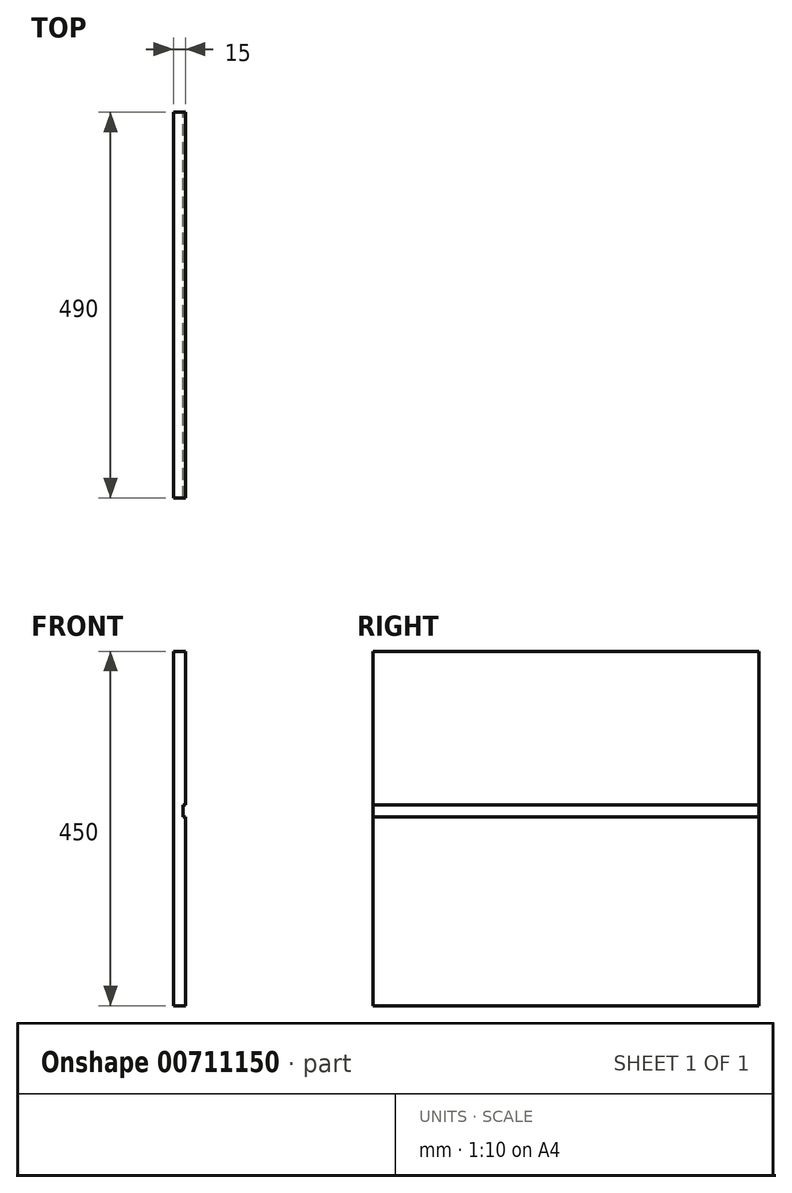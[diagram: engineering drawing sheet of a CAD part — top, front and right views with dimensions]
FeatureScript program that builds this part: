
annotation { "Feature Type Name" : "Feature", "Feature Type Description" : "" }
export const myFeature = defineFeature(function(context is Context, id is Id, definition is map)
    precondition{}
    {
        {
            var Q0;
            Q0=qCreatedBy(makeId("Right.planeOp"),FACE);
            var sketch = newSketch(context, id + "F0", { "sketchPlane" : qUnion([Q0])});
            skLineSegment(sketch, "E0.bottom", {"start": v(0, 0) * mm, "end": v(490, 0) * mm});
            skLineSegment(sketch, "E0.top", {"start": v(0, 450) * mm, "end": v(490, 450) * mm});
            skLineSegment(sketch, "E0.left", {"start": v(0, 0) * mm, "end": v(0, 450) * mm});
            skLineSegment(sketch, "E0.right", {"start": v(490, 0) * mm, "end": v(490, 450) * mm});
            skSolve(sketch);
        }
        {
            var Q0;
            Q0=makeQuery(id+"F0.imprint","IMPRINT",FACE,{"disambiguationData":[TD([[makeQuery(id+"F0.imprint","IMPRINT",EDGE,{"derivedFrom":sQuery(id+"F0.wireOp",EDGE,"E0.bottom")}),1.0]])]});
            extrude(context, id + "F1", {"entities" : qUnion([Q0]), "depth" : 15 * mm, "offsetDistance" : 25 * mm});
        }
        {
            var Q0;
            Q0=makeQuery(id+"F1.opExtrude","CAP_FACE",FACE,{"disambiguationData":[OSD([sQuery(id+"F0.wireOp",EDGE,"E0.bottom"),sQuery(id+"F0.wireOp",EDGE,"E0.top"),sQuery(id+"F0.wireOp",EDGE,"E0.left"),sQuery(id+"F0.wireOp",EDGE,"E0.right")])],"isStart":false});
            var sketch = newSketch(context, id + "F2", { "sketchPlane" : qUnion([Q0])});
            skLineSegment(sketch, "E1.bottom", {"start": v(0, 255) * mm, "end": v(490, 255) * mm});
            skLineSegment(sketch, "E1.top", {"start": v(0, 240) * mm, "end": v(490, 240) * mm});
            skLineSegment(sketch, "E1.left", {"start": v(0, 255) * mm, "end": v(0, 240) * mm});
            skLineSegment(sketch, "E1.right", {"start": v(490, 255) * mm, "end": v(490, 240) * mm});
            skLineSegment(sketch, "E2", {"start": v(0, 240) * mm, "end": v(0, 0) * mm});
            skSolve(sketch);
        }
        {
            var Q0;
            Q0=makeQuery(id+"F2.imprint","IMPRINT",FACE,{"disambiguationData":[TD([[makeQuery(id+"F2.imprint","IMPRINT",EDGE,{"derivedFrom":sQuery(id+"F2.wireOp",EDGE,"E1.bottom")}),-1.0]])]});
            extrude(context, id + "F3", {"entities" : qUnion([Q0]), "operationType" : NewBodyOperationType.REMOVE, "oppositeDirection" : true, "depth" : 3 * mm, "offsetDistance" : 25 * mm});
        }
    });
